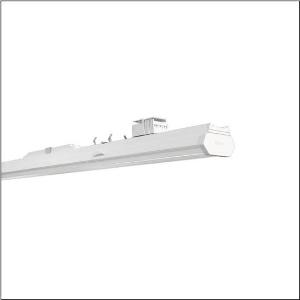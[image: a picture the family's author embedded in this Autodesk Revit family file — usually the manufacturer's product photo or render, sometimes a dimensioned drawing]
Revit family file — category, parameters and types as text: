
# Revit family: licross_r__11_protected_mo_51tp12dn495g3s_1208
name_source: partatom
category: Lighting Fixtures
units: mm (PartAtom-declared; Revit-internal decimal feet)

## family parameters
Cut with Voids When Loaded = No
Host = Face
Light Source = No
Part Type = Normal
Room Calculation Point = No
Round Connector Dimension = Use Diameter
Shared = No

## types (1)
- --- (1 x LED, 980 lm, 6.8 W, 4000K)
    Apparent Load = 7 VA
    CIE Flux Codes = 73 92 98 99 100
    Color Rendering = 80
    Color Temperature = 4000K
    Default Elevation = 1800 mm
    Description = Licross® 11 Protected MO, luminaire insert, of sheet steel, galvanised, coil coated, white, length: 1.500mm, width: 90mm, height: 101mm, LED rated luminous flux: 9.980lm, light colour: 840, SDCM (Standard Deviation of Colour Matching)MacAdam ≤ 2 SDCM (initial), control gear: DALI 2 (for two DALI lines), with plug, 6-pole, with phase selection, for trunking rail, 14-core, mains connection: 220..240V, AC, 50/60Hz, rated input power: 61W, for trunking rail, 14-core, internal wiring halogen-free, for emergency light function, converter,control gear: single battery element, battery: LiFePO4, 9Ah, primary light control with lens, of plastic, primary optical cover: cover, of PMMA, light emission: direct distribution, primary light characteristic: symmetric, protection rating (complete): IP64, insulation class (complete): insulation class I (protective earthing), certification: CE, UKCA, protection symbol: D if used in an environment with conductive dust loads with corresponding accessories, impact resistance: IK06, permissible ambient temperature for indoor applications: +5..+35°C, standard: EN 60598-2-22, LABS conformity tested according to VDMA 24364:2018-05, reducing of maximum allowable ambient temperature of 5°C with ceiling mounting, corresponds to IFS (International Featured Standards) requirements for safety and quality in the food industry, packaging unit: 1 piece
    Height = 92 mm
    Lamp = 1 x LED
    Lamp Light Flux = 980 lm
    Lamp Power = 6.8 W
    Lamp count = 1
    Length = 1500 mm
    Luminous efficacy = 144 lm/W
    Manufacturer = Siteco
    ModVariant = No
    Model = 51TP12DN495G3S
    Mounting Place = Ceiling
    Mounting Type = Pendant
    Number of Poles = 1
    OnlyDefault = Yes
    Power Factor = 1
    Product Name = Licross® 11 Protected MO
    Product group = luminaire insert | ceiling pendant
    ProductGroupID = 901
    Protection Class = Protection class I
    Protection Degree = IP 64
    RLX_Detail_Level = 1
    RLX_Emergency_Light_Flux = 0 lm
    RLX_Emergency_Type = 0
    RLX_Emergency_Type_DB = No
    RlxData = <blob elided: 24781 chars, md5=82485914>
    Socket = socket
    Standby Power = 0 W
    System Light Flux = 980 lm
    System Power = 7 W
    Type Comments = : emergency light operation: 3 h
    Type Image = l_1256148.jpg
    URL = http://relux.com
    VarID = @adj_098527
    Voltage = 0 V
    Weight = 0.00 kg
    Width = 88 mm

## geometry (parser evidence)
native form markers: Blend x4, Sweep x12
no freeform markers — native parametric forms only
